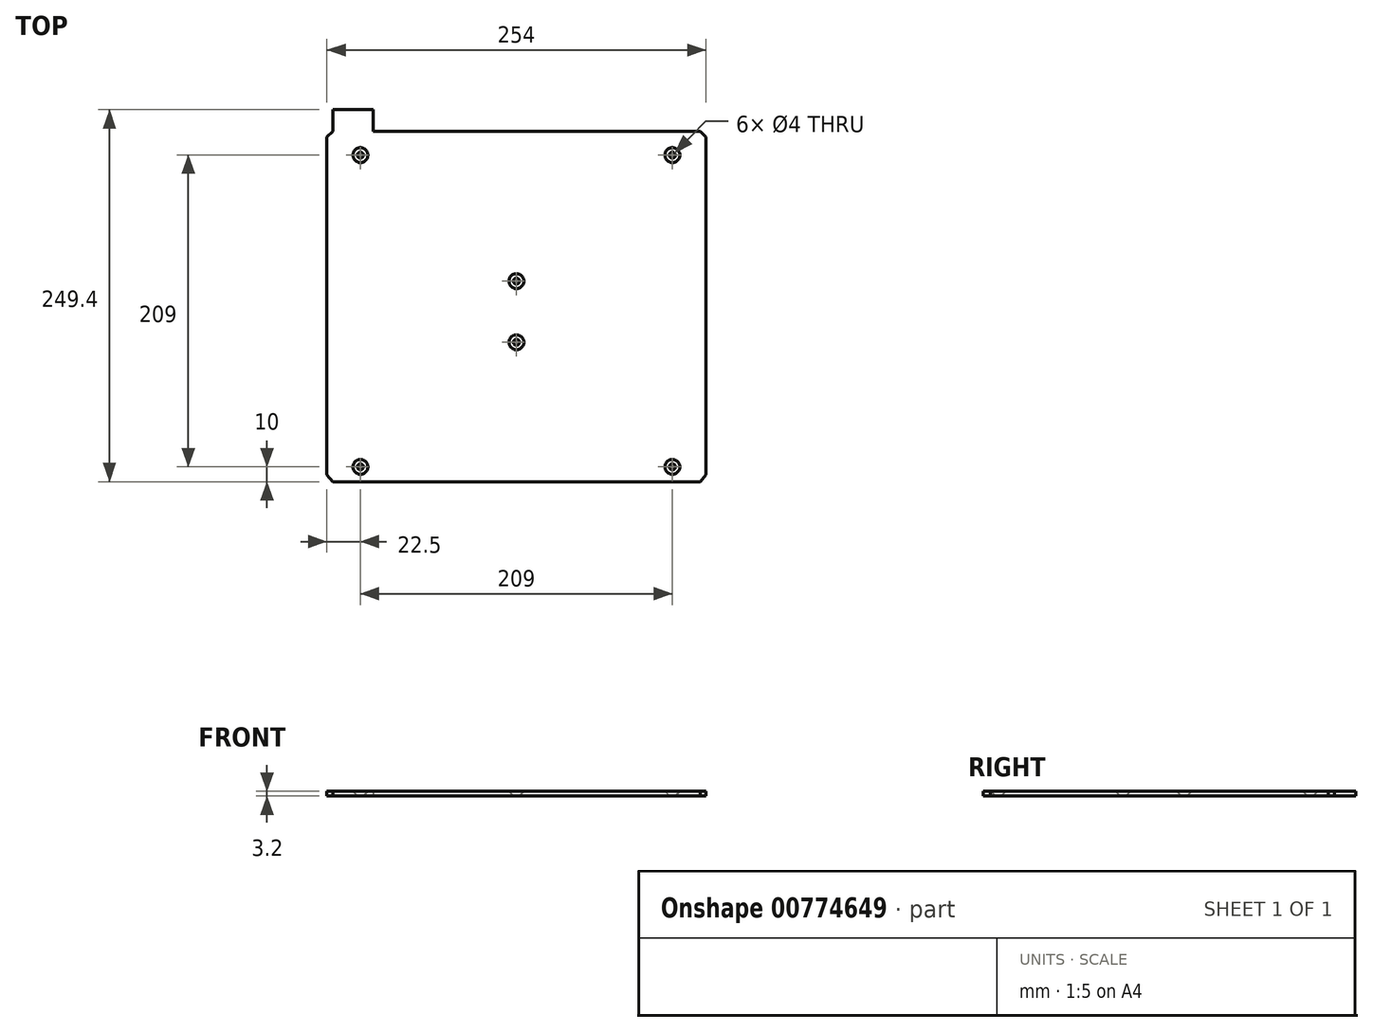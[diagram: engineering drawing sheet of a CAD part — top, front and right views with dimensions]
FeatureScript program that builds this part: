
annotation { "Feature Type Name" : "Feature", "Feature Type Description" : "" }
export const myFeature = defineFeature(function(context is Context, id is Id, definition is map)
    precondition{}
    {
        {
            var Q0;
            Q0=qCreatedBy(makeId("Top.planeOp"),FACE);
            var sketch = newSketch(context, id + "F0", { "sketchPlane" : qUnion([Q0])});
            skLineSegment(sketch, "E0", {"start": v(-123, 131.9) * mm, "end": v(-123, 117.5) * mm});
            skLineSegment(sketch, "E1", {"start": v(-123, 117.5) * mm, "end": v(-127, 113.5) * mm});
            skLineSegment(sketch, "E2", {"start": v(-127, 113.5) * mm, "end": v(-127, -112.73) * mm});
            skLineSegment(sketch, "E3", {"start": v(-127, -112.73) * mm, "end": v(-123, -117.5) * mm});
            skLineSegment(sketch, "E4", {"start": v(-123, -117.5) * mm, "end": v(123, -117.5) * mm});
            skLineSegment(sketch, "E5", {"start": v(123, -117.5) * mm, "end": v(127, -112.73) * mm});
            skLineSegment(sketch, "E6", {"start": v(127, -112.73) * mm, "end": v(127, 113.5) * mm});
            skLineSegment(sketch, "E7", {"start": v(127, 113.5) * mm, "end": v(123, 117.5) * mm});
            skLineSegment(sketch, "E8", {"start": v(123, 117.5) * mm, "end": v(-96, 117.5) * mm});
            skLineSegment(sketch, "E9", {"start": v(-96, 117.5) * mm, "end": v(-96, 131.9) * mm});
            skLineSegment(sketch, "E10", {"start": v(-96, 131.9) * mm, "end": v(-123, 131.9) * mm});
            skCircle(sketch, "E11", {"center": v(-104.5, -107.5) * mm, "radius": 2 * mm});
            skCircle(sketch, "E12", {"center": v(-104.5, 101.5) * mm, "radius": 2 * mm});
            skCircle(sketch, "E13", {"center": v(0, 17) * mm, "radius": 2 * mm});
            skCircle(sketch, "E14", {"center": v(0, -24) * mm, "radius": 2 * mm});
            skCircle(sketch, "E15", {"center": v(104.5, 101.5) * mm, "radius": 2 * mm});
            skCircle(sketch, "E16", {"center": v(104.5, -107.5) * mm, "radius": 2 * mm});
            skSolve(sketch);
        }
        {
            var Q0;
            Q0 = qSketchRegion(id + "F0", true);
            extrude(context, id + "F1", {"entities" : qUnion([Q0]), "depth" : 3.2 * mm, "offsetDistance" : 25 * mm});
        }
        {
            var Q0;
            Q0=makeQuery(id+"F1.opExtrude","CAP_EDGE",EDGE,{"disambiguationData":[OSD([sQuery(id+"F0.wireOp",EDGE,"E12")])],"isStart":false});
            var Q1;
            Q1=makeQuery(id+"F1.opExtrude","CAP_EDGE",EDGE,{"disambiguationData":[OSD([sQuery(id+"F0.wireOp",EDGE,"E13")])],"isStart":false});
            var Q2;
            Q2=makeQuery(id+"F1.opExtrude","CAP_EDGE",EDGE,{"disambiguationData":[OSD([sQuery(id+"F0.wireOp",EDGE,"E14")])],"isStart":false});
            var Q3;
            Q3=makeQuery(id+"F1.opExtrude","CAP_EDGE",EDGE,{"disambiguationData":[OSD([sQuery(id+"F0.wireOp",EDGE,"E15")])],"isStart":false});
            var Q4;
            Q4=makeQuery(id+"F1.opExtrude","CAP_EDGE",EDGE,{"disambiguationData":[OSD([sQuery(id+"F0.wireOp",EDGE,"E16")])],"isStart":false});
            var Q5;
            Q5=makeQuery(id+"F1.opExtrude","CAP_EDGE",EDGE,{"disambiguationData":[OSD([sQuery(id+"F0.wireOp",EDGE,"E11")])],"isStart":false});
            chamfer(context, id + "F2", {"entities" : qUnion([Q0, Q1, Q2, Q3, Q4, Q5]), "width" : 3 * mm, "tangentPropagation" : true});
        }
    });
